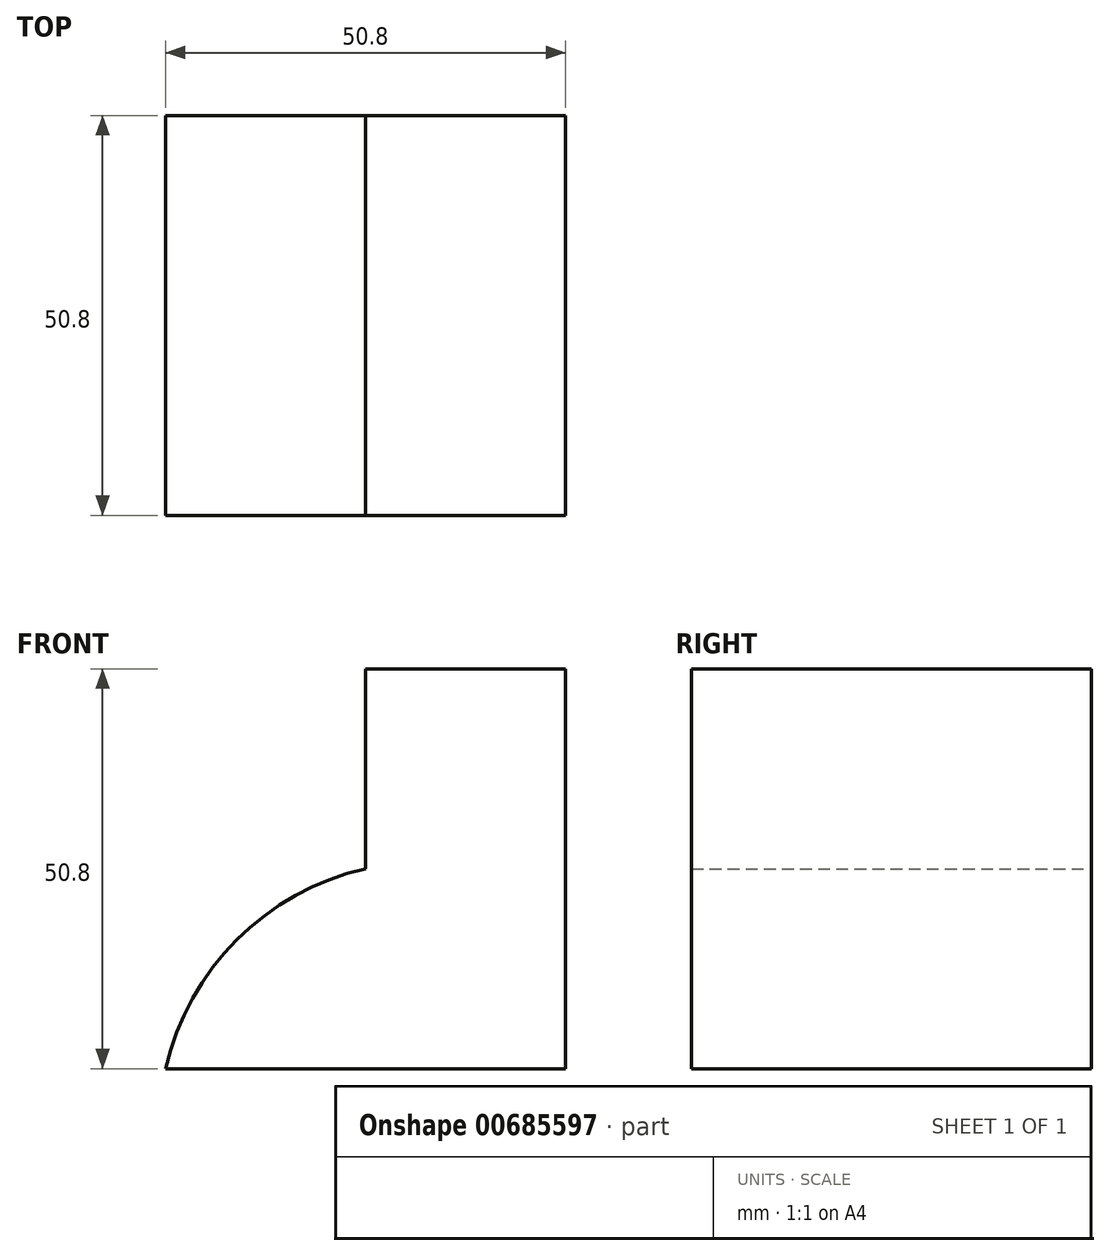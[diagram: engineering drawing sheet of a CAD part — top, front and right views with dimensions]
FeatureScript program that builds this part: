
annotation { "Feature Type Name" : "Feature", "Feature Type Description" : "" }
export const myFeature = defineFeature(function(context is Context, id is Id, definition is map)
    precondition{}
    {
        {
            var Q0;
            Q0=qCreatedBy(makeId("Front.planeOp"),FACE);
            var sketch = newSketch(context, id + "F0", { "sketchPlane" : qUnion([Q0])});
            skLineSegment(sketch, "E0", {"start": v(0, 0) * mm, "end": v(50.8, 0) * mm});
            skLineSegment(sketch, "E1", {"start": v(50.8, 0) * mm, "end": v(50.8, 50.8) * mm});
            skLineSegment(sketch, "E2", {"start": v(50.8, 50.8) * mm, "end": v(25.4, 50.8) * mm});
            skLineSegment(sketch, "E3", {"start": v(25.4, 50.8) * mm, "end": v(25.4, 25.4) * mm});
            skArc(sketch, "E4", {"start": v(25.4, 25.4) * mm, "mid": v(9.04, 16.36) * mm, "end": v(0, 0) * mm});
            skSolve(sketch);
        }
        {
            var Q0;
            Q0 = qSketchRegion(id + "F0", true);
            extrude(context, id + "F1", {"entities" : qUnion([Q0]), "depth" : 50.8 * mm, "offsetDistance" : 25.4 * mm});
        }
    });
